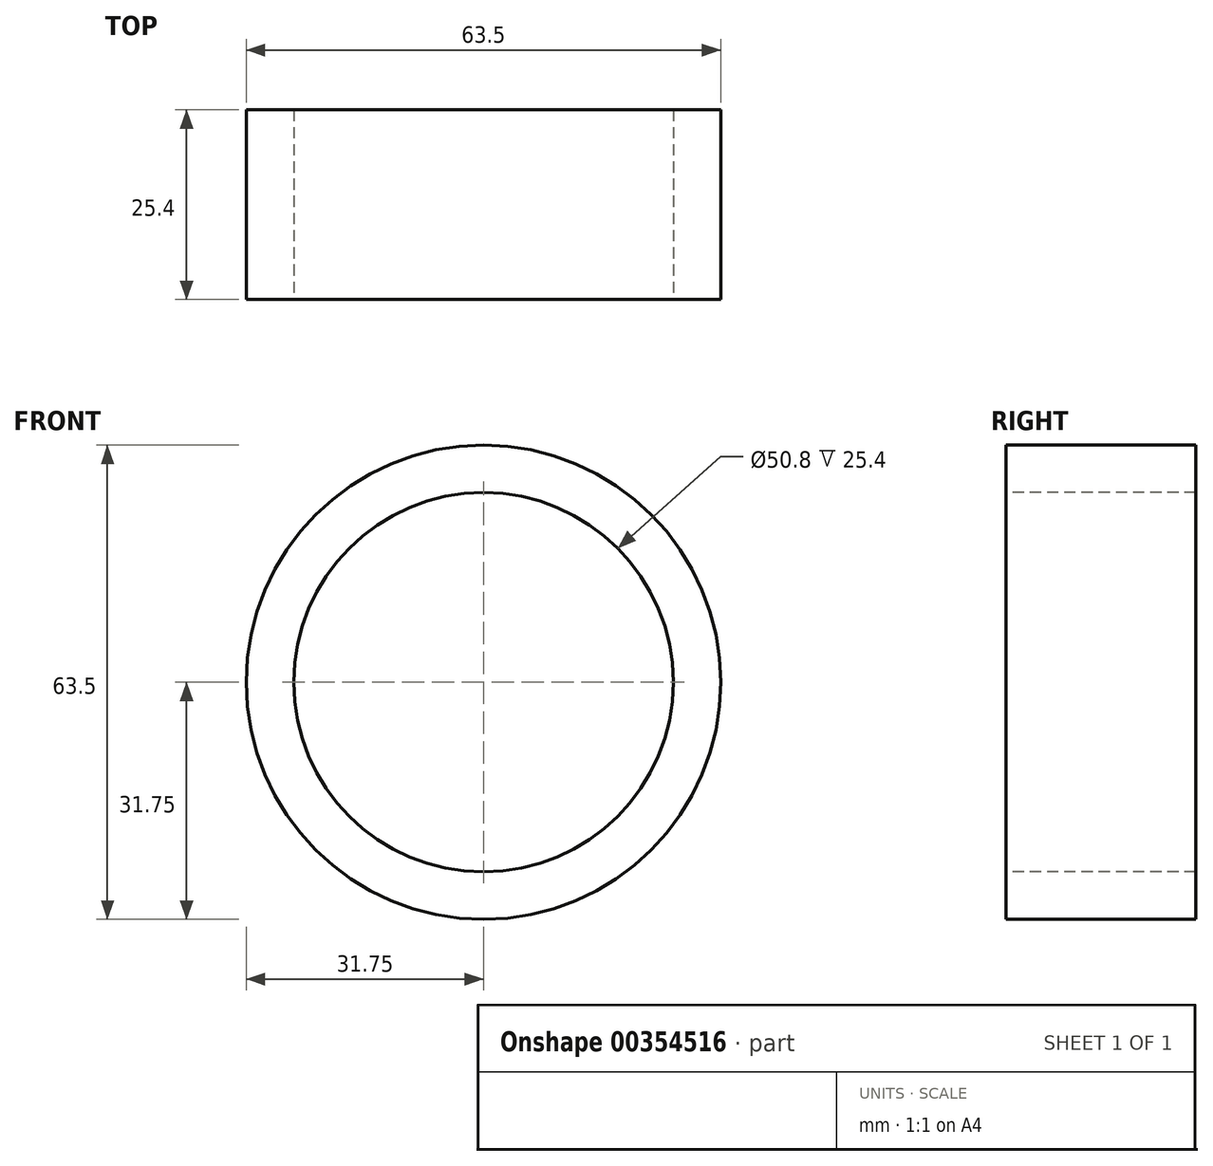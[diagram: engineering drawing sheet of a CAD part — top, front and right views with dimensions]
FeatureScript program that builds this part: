
annotation { "Feature Type Name" : "Feature", "Feature Type Description" : "" }
export const myFeature = defineFeature(function(context is Context, id is Id, definition is map)
    precondition{}
    {
        {
            var Q0;
            Q0=qCreatedBy(makeId("Front.planeOp"),FACE);
            var sketch = newSketch(context, id + "F0", { "sketchPlane" : qUnion([Q0])});
            skCircle(sketch, "E0", {"center": v(0, 0) * mm, "radius": 31.75 * mm});
            skCircle(sketch, "E1", {"center": v(0, 0) * mm, "radius": 25.4 * mm});
            skSolve(sketch);
        }
        {
            var Q0;
            Q0 = qSketchRegion(id + "F0", true);
            extrude(context, id + "F1", {"entities" : qUnion([Q0]), "oppositeDirection" : true, "depth" : 25.4 * mm});
        }
    });
